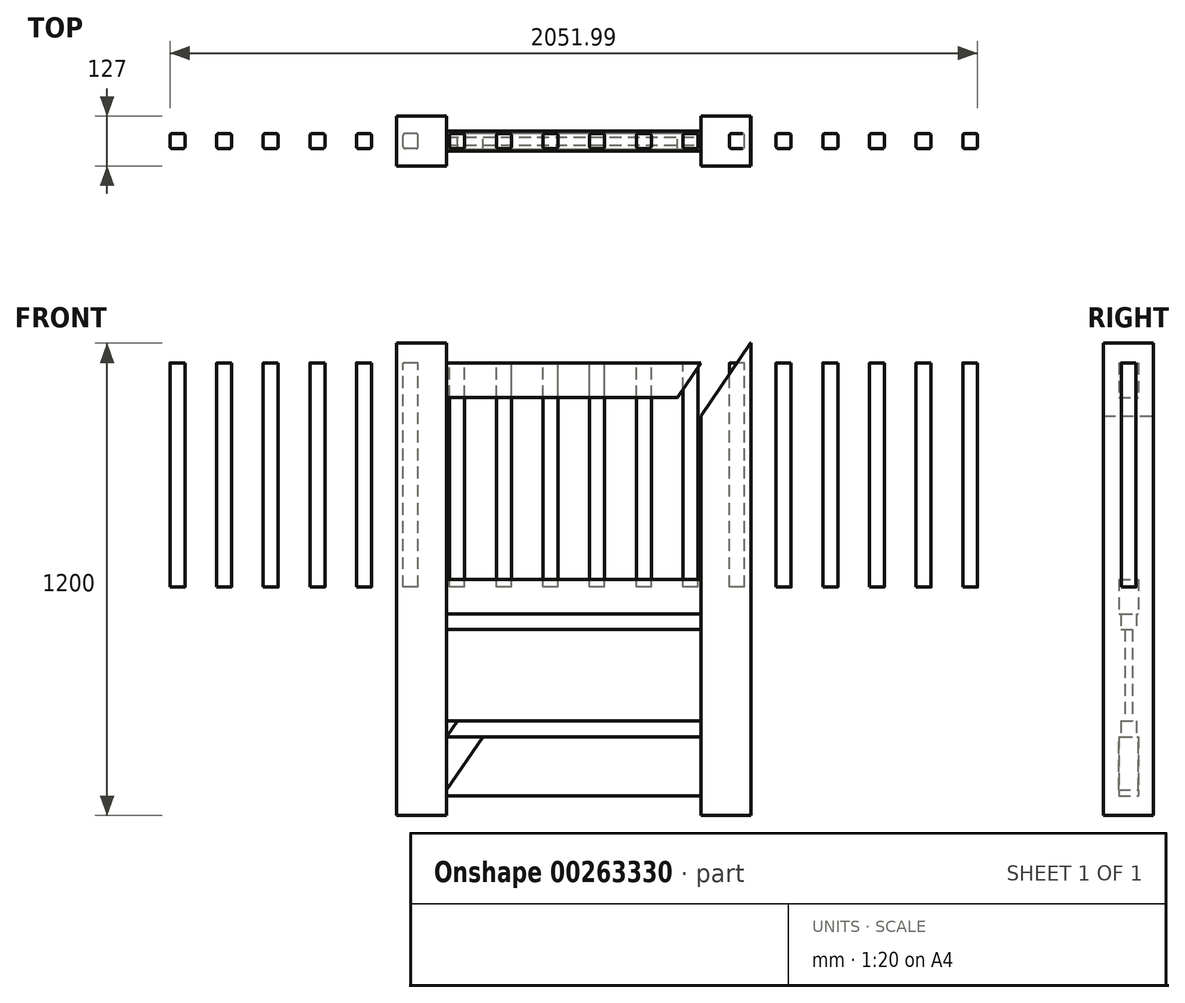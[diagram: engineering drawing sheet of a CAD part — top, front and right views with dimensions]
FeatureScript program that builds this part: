
annotation { "Feature Type Name" : "Feature", "Feature Type Description" : "" }
export const myFeature = defineFeature(function(context is Context, id is Id, definition is map)
    precondition{}
    {
        {
            var Q0;
            Q0=qCreatedBy(makeId("Front.planeOp"),FACE);
            var sketch = newSketch(context, id + "F0", { "sketchPlane" : qUnion([Q0])});
            skLineSegment(sketch, "E0.bottom", {"start": v(450, -600) * mm, "end": v(323, -600) * mm});
            skLineSegment(sketch, "E0.top", {"start": v(450, 600) * mm, "end": v(323, 600) * mm});
            skLineSegment(sketch, "E0.left", {"start": v(450, -600) * mm, "end": v(450, 600) * mm});
            skLineSegment(sketch, "E0.right", {"start": v(-450, -600) * mm, "end": v(-450, 600) * mm});
            skPoint(sketch, "E0.middle", {"position": v(0, 0) * mm});
            skLineSegment(sketch, "E1", {"start": v(-323, 600) * mm, "end": v(-323, -600) * mm});
            skLineSegment(sketch, "E2", {"start": v(323, 600) * mm, "end": v(323, -600) * mm});
            skLineSegment(sketch, "E3", {"start": v(-323, 550) * mm, "end": v(323, 550) * mm});
            skLineSegment(sketch, "E4", {"start": v(-323, 462) * mm, "end": v(323, 462) * mm});
            skLineSegment(sketch, "E5.trimOffspring", {"start": v(-323, 600) * mm, "end": v(-450, 600) * mm});
            skLineSegment(sketch, "E6", {"start": v(-323, 0) * mm, "end": v(323, 0) * mm});
            skLineSegment(sketch, "E7", {"start": v(-323, -88) * mm, "end": v(323, -88) * mm});
            skLineSegment(sketch, "E8", {"start": v(-323, -550) * mm, "end": v(323, -550) * mm});
            skLineSegment(sketch, "E9", {"start": v(-323, -400) * mm, "end": v(323, -400) * mm});
            skLineSegment(sketch, "E10.trimOffspring", {"start": v(-323, -600) * mm, "end": v(-450, -600) * mm});
            skLineSegment(sketch, "E11", {"start": v(-323, -360) * mm, "end": v(323, -360) * mm});
            skLineSegment(sketch, "E12", {"start": v(-323, -128) * mm, "end": v(323, -128) * mm});
            skLineSegment(sketch, "E13", {"start": v(323, 550) * mm, "end": v(-323, -400) * mm});
            skLineSegment(sketch, "E14", {"start": v(-323, -535.16) * mm, "end": v(526.29, 713.8) * mm});
            skSolve(sketch);
        }
        {
            var Q0;
            Q0=makeQuery(id+"F0.imprint","IMPRINT",FACE,{"disambiguationData":[TD([[makeQuery(id+"F0.imprint","IMPRINT",EDGE,{"derivedFrom":sQuery(id+"F0.wireOp",EDGE,"E0.right")}),-1.0]])]});
            var Q1;
            {var subQ8=sQuery(id+"F0.wireOp",EDGE,"E0.bottom");Q1=makeQuery(id+"F0.imprint","IMPRINT",FACE,{"disambiguationData":[TD([[makeQuery(id+"F0.imprint","IMPRINT",EDGE,{"derivedFrom":subQ8}),-1.0]])]});}
            extrude(context, id + "F1", {"entities" : qUnion([Q0, Q1]), "depth" : 63.5 * mm, "hasSecondDirection" : true, "secondDirectionOppositeDirection" : true, "secondDirectionDepth" : 63.5 * mm});
        }
        {
            var Q0;
            {var subQ0=sQuery(id+"F0.wireOp",EDGE,"E8");Q0=makeQuery(id+"F0.imprint","IMPRINT",FACE,{"disambiguationData":[TD([[makeQuery(id+"F0.imprint","IMPRINT",EDGE,{"derivedFrom":subQ0}),1.0]])]});}
            var Q1;
            {var subQ0=sQuery(id+"F0.wireOp",EDGE,"E3");Q1=makeQuery(id+"F0.imprint","IMPRINT",FACE,{"disambiguationData":[TD([[makeQuery(id+"F0.imprint","IMPRINT",EDGE,{"derivedFrom":subQ0}),-1.0]])]});}
            var Q2;
            {var subQ0=sQuery(id+"F0.wireOp",EDGE,"E6");Q2=makeQuery(id+"F0.imprint","IMPRINT",FACE,{"disambiguationData":[TD([[makeQuery(id+"F0.imprint","IMPRINT",EDGE,{"derivedFrom":subQ0}),-1.0]])]});}
            extrude(context, id + "F2", {"entities" : qUnion([Q0, Q1, Q2]), "depth" : 25 * mm, "hasSecondDirection" : true, "secondDirectionOppositeDirection" : true, "secondDirectionDepth" : 25 * mm});
        }
        {
            var Q0;
            {var subQ0=sQuery(id+"F0.wireOp",EDGE,"E7");Q0=makeQuery(id+"F0.imprint","IMPRINT",FACE,{"disambiguationData":[TD([[makeQuery(id+"F0.imprint","IMPRINT",EDGE,{"derivedFrom":subQ0}),-1.0]])]});}
            var Q1;
            {var subQ0=sQuery(id+"F0.wireOp",EDGE,"E9");Q1=makeQuery(id+"F0.imprint","IMPRINT",FACE,{"disambiguationData":[TD([[makeQuery(id+"F0.imprint","IMPRINT",EDGE,{"derivedFrom":subQ0}),1.0]])]});}
            extrude(context, id + "F3", {"entities" : qUnion([Q0, Q1]), "depth" : 20 * mm, "hasSecondDirection" : true, "secondDirectionOppositeDirection" : true, "secondDirectionDepth" : 20 * mm});
        }
        {
            var Q0;
            {var subQ0=sQuery(id+"F0.wireOp",EDGE,"E11");Q0=makeQuery(id+"F0.imprint","IMPRINT",FACE,{"disambiguationData":[TD([[makeQuery(id+"F0.imprint","IMPRINT",EDGE,{"derivedFrom":subQ0}),1.0]])]});}
            extrude(context, id + "F4", {"entities" : qUnion([Q0]), "depth" : 10 * mm, "hasSecondDirection" : true, "secondDirectionOppositeDirection" : true, "secondDirectionDepth" : 10 * mm});
        }
        {
            var Q0;
            Q0=makeQuery(id+"F2.opExtrude","SWEPT_FACE",FACE,{"disambiguationData":[OSD([sQuery(id+"F0.wireOp",EDGE,"E3")])]});
            var sketch = newSketch(context, id + "F5", { "sketchPlane" : qUnion([Q0])});
            skLineSegment(sketch, "E15.bottom", {"start": v(-993.03, -19) * mm, "end": v(-1021.03, -19) * mm});
            skLineSegment(sketch, "E15.top", {"start": v(-993.03, 19) * mm, "end": v(-1021.03, 19) * mm});
            skLineSegment(sketch, "E15.left", {"start": v(-988.03, -14) * mm, "end": v(-988.03, 14) * mm});
            skLineSegment(sketch, "E15.right", {"start": v(-1026.03, -14) * mm, "end": v(-1026.03, 14) * mm});
            skPoint(sketch, "E15.middle", {"position": v(-1007.03, 0) * mm});
            skPoint(sketch, "E16.visualSharp", {"position": v(-1026.03, 19) * mm});
            skArc(sketch, "E16.filletArc", {"start": v(-1021.03, 19) * mm, "mid": v(-1024.57, 17.54) * mm, "end": v(-1026.03, 14) * mm});
            skPoint(sketch, "E17.visualSharp", {"position": v(-1026.03, -19) * mm});
            skArc(sketch, "E17.filletArc", {"start": v(-1026.03, -14) * mm, "mid": v(-1024.57, -17.54) * mm, "end": v(-1021.03, -19) * mm});
            skPoint(sketch, "E18.visualSharp", {"position": v(-988.03, -19) * mm});
            skArc(sketch, "E18.filletArc", {"start": v(-993.03, -19) * mm, "mid": v(-989.5, -17.54) * mm, "end": v(-988.03, -14) * mm});
            skPoint(sketch, "E19.visualSharp", {"position": v(-988.03, 19) * mm});
            skArc(sketch, "E19.filletArc", {"start": v(-988.03, 14) * mm, "mid": v(-989.5, 17.54) * mm, "end": v(-993.03, 19) * mm});
            skLineSegment(sketch, "E20.1.0.0", {"start": v(-874.56, 19) * mm, "end": v(-902.56, 19) * mm});
            skArc(sketch, "E20.1.0.1", {"start": v(-902.56, 19) * mm, "mid": v(-906.1, 17.54) * mm, "end": v(-907.56, 14) * mm});
            skLineSegment(sketch, "E20.1.0.2", {"start": v(-907.56, -14) * mm, "end": v(-907.56, 14) * mm});
            skArc(sketch, "E20.1.0.3", {"start": v(-907.56, -14) * mm, "mid": v(-906.1, -17.54) * mm, "end": v(-902.56, -19) * mm});
            skLineSegment(sketch, "E20.1.0.4", {"start": v(-874.56, -19) * mm, "end": v(-902.56, -19) * mm});
            skArc(sketch, "E20.1.0.5", {"start": v(-874.56, -19) * mm, "mid": v(-871.02, -17.54) * mm, "end": v(-869.56, -14) * mm});
            skLineSegment(sketch, "E20.1.0.6", {"start": v(-869.56, -14) * mm, "end": v(-869.56, 14) * mm});
            skArc(sketch, "E20.1.0.7", {"start": v(-869.56, 14) * mm, "mid": v(-871.02, 17.54) * mm, "end": v(-874.56, 19) * mm});
            skLineSegment(sketch, "E20.2.0.0", {"start": v(-756.1, 19) * mm, "end": v(-784.1, 19) * mm});
            skArc(sketch, "E20.2.0.1", {"start": v(-784.1, 19) * mm, "mid": v(-787.63, 17.54) * mm, "end": v(-789.1, 14) * mm});
            skLineSegment(sketch, "E20.2.0.2", {"start": v(-789.1, -14) * mm, "end": v(-789.1, 14) * mm});
            skArc(sketch, "E20.2.0.3", {"start": v(-789.1, -14) * mm, "mid": v(-787.63, -17.54) * mm, "end": v(-784.1, -19) * mm});
            skLineSegment(sketch, "E20.2.0.4", {"start": v(-756.1, -19) * mm, "end": v(-784.1, -19) * mm});
            skArc(sketch, "E20.2.0.5", {"start": v(-756.1, -19) * mm, "mid": v(-752.55, -17.54) * mm, "end": v(-751.1, -14) * mm});
            skLineSegment(sketch, "E20.2.0.6", {"start": v(-751.1, -14) * mm, "end": v(-751.1, 14) * mm});
            skArc(sketch, "E20.2.0.7", {"start": v(-751.1, 14) * mm, "mid": v(-752.55, 17.54) * mm, "end": v(-756.1, 19) * mm});
            skLineSegment(sketch, "E20.3.0.0", {"start": v(-637.62, 19) * mm, "end": v(-665.62, 19) * mm});
            skArc(sketch, "E20.3.0.1", {"start": v(-665.62, 19) * mm, "mid": v(-669.16, 17.54) * mm, "end": v(-670.62, 14) * mm});
            skLineSegment(sketch, "E20.3.0.2", {"start": v(-670.62, -14) * mm, "end": v(-670.62, 14) * mm});
            skArc(sketch, "E20.3.0.3", {"start": v(-670.62, -14) * mm, "mid": v(-669.16, -17.54) * mm, "end": v(-665.62, -19) * mm});
            skLineSegment(sketch, "E20.3.0.4", {"start": v(-637.62, -19) * mm, "end": v(-665.62, -19) * mm});
            skArc(sketch, "E20.3.0.5", {"start": v(-637.62, -19) * mm, "mid": v(-634.08, -17.54) * mm, "end": v(-632.62, -14) * mm});
            skLineSegment(sketch, "E20.3.0.6", {"start": v(-632.62, -14) * mm, "end": v(-632.62, 14) * mm});
            skArc(sketch, "E20.3.0.7", {"start": v(-632.62, 14) * mm, "mid": v(-634.08, 17.54) * mm, "end": v(-637.62, 19) * mm});
            skLineSegment(sketch, "E20.4.0.0", {"start": v(-519.15, 19) * mm, "end": v(-547.15, 19) * mm});
            skArc(sketch, "E20.4.0.1", {"start": v(-547.15, 19) * mm, "mid": v(-550.69, 17.54) * mm, "end": v(-552.15, 14) * mm});
            skLineSegment(sketch, "E20.4.0.2", {"start": v(-552.15, -14) * mm, "end": v(-552.15, 14) * mm});
            skArc(sketch, "E20.4.0.3", {"start": v(-552.15, -14) * mm, "mid": v(-550.69, -17.54) * mm, "end": v(-547.15, -19) * mm});
            skLineSegment(sketch, "E20.4.0.4", {"start": v(-519.15, -19) * mm, "end": v(-547.15, -19) * mm});
            skArc(sketch, "E20.4.0.5", {"start": v(-519.15, -19) * mm, "mid": v(-515.61, -17.54) * mm, "end": v(-514.15, -14) * mm});
            skLineSegment(sketch, "E20.4.0.6", {"start": v(-514.15, -14) * mm, "end": v(-514.15, 14) * mm});
            skArc(sketch, "E20.4.0.7", {"start": v(-514.15, 14) * mm, "mid": v(-515.61, 17.54) * mm, "end": v(-519.15, 19) * mm});
            skLineSegment(sketch, "E20.5.0.0", {"start": v(-400.68, 19) * mm, "end": v(-428.68, 19) * mm});
            skArc(sketch, "E20.5.0.1", {"start": v(-428.68, 19) * mm, "mid": v(-432.22, 17.54) * mm, "end": v(-433.68, 14) * mm});
            skLineSegment(sketch, "E20.5.0.2", {"start": v(-433.68, -14) * mm, "end": v(-433.68, 14) * mm});
            skArc(sketch, "E20.5.0.3", {"start": v(-433.68, -14) * mm, "mid": v(-432.22, -17.54) * mm, "end": v(-428.68, -19) * mm});
            skLineSegment(sketch, "E20.5.0.4", {"start": v(-400.68, -19) * mm, "end": v(-428.68, -19) * mm});
            skArc(sketch, "E20.5.0.5", {"start": v(-400.68, -19) * mm, "mid": v(-397.14, -17.54) * mm, "end": v(-395.68, -14) * mm});
            skLineSegment(sketch, "E20.5.0.6", {"start": v(-395.68, -14) * mm, "end": v(-395.68, 14) * mm});
            skArc(sketch, "E20.5.0.7", {"start": v(-395.68, 14) * mm, "mid": v(-397.14, 17.54) * mm, "end": v(-400.68, 19) * mm});
            skLineSegment(sketch, "E20.6.0.0", {"start": v(-282.21, 19) * mm, "end": v(-310.21, 19) * mm});
            skArc(sketch, "E20.6.0.1", {"start": v(-310.21, 19) * mm, "mid": v(-313.75, 17.54) * mm, "end": v(-315.21, 14) * mm});
            skLineSegment(sketch, "E20.6.0.2", {"start": v(-315.21, -14) * mm, "end": v(-315.21, 14) * mm});
            skArc(sketch, "E20.6.0.3", {"start": v(-315.21, -14) * mm, "mid": v(-313.75, -17.54) * mm, "end": v(-310.21, -19) * mm});
            skLineSegment(sketch, "E20.6.0.4", {"start": v(-282.21, -19) * mm, "end": v(-310.21, -19) * mm});
            skArc(sketch, "E20.6.0.5", {"start": v(-282.21, -19) * mm, "mid": v(-278.67, -17.54) * mm, "end": v(-277.21, -14) * mm});
            skLineSegment(sketch, "E20.6.0.6", {"start": v(-277.21, -14) * mm, "end": v(-277.21, 14) * mm});
            skArc(sketch, "E20.6.0.7", {"start": v(-277.21, 14) * mm, "mid": v(-278.67, 17.54) * mm, "end": v(-282.21, 19) * mm});
            skLineSegment(sketch, "E20.7.0.0", {"start": v(-163.74, 19) * mm, "end": v(-191.74, 19) * mm});
            skArc(sketch, "E20.7.0.1", {"start": v(-191.74, 19) * mm, "mid": v(-195.28, 17.54) * mm, "end": v(-196.74, 14) * mm});
            skLineSegment(sketch, "E20.7.0.2", {"start": v(-196.74, -14) * mm, "end": v(-196.74, 14) * mm});
            skArc(sketch, "E20.7.0.3", {"start": v(-196.74, -14) * mm, "mid": v(-195.28, -17.54) * mm, "end": v(-191.74, -19) * mm});
            skLineSegment(sketch, "E20.7.0.4", {"start": v(-163.74, -19) * mm, "end": v(-191.74, -19) * mm});
            skArc(sketch, "E20.7.0.5", {"start": v(-163.74, -19) * mm, "mid": v(-160.2, -17.54) * mm, "end": v(-158.74, -14) * mm});
            skLineSegment(sketch, "E20.7.0.6", {"start": v(-158.74, -14) * mm, "end": v(-158.74, 14) * mm});
            skArc(sketch, "E20.7.0.7", {"start": v(-158.74, 14) * mm, "mid": v(-160.2, 17.54) * mm, "end": v(-163.74, 19) * mm});
            skLineSegment(sketch, "E20.8.0.0", {"start": v(-45.27, 19) * mm, "end": v(-73.27, 19) * mm});
            skArc(sketch, "E20.8.0.1", {"start": v(-73.27, 19) * mm, "mid": v(-76.8, 17.54) * mm, "end": v(-78.27, 14) * mm});
            skLineSegment(sketch, "E20.8.0.2", {"start": v(-78.27, -14) * mm, "end": v(-78.27, 14) * mm});
            skArc(sketch, "E20.8.0.3", {"start": v(-78.27, -14) * mm, "mid": v(-76.8, -17.54) * mm, "end": v(-73.27, -19) * mm});
            skLineSegment(sketch, "E20.8.0.4", {"start": v(-45.27, -19) * mm, "end": v(-73.27, -19) * mm});
            skArc(sketch, "E20.8.0.5", {"start": v(-45.27, -19) * mm, "mid": v(-41.73, -17.54) * mm, "end": v(-40.27, -14) * mm});
            skLineSegment(sketch, "E20.8.0.6", {"start": v(-40.27, -14) * mm, "end": v(-40.27, 14) * mm});
            skArc(sketch, "E20.8.0.7", {"start": v(-40.27, 14) * mm, "mid": v(-41.73, 17.54) * mm, "end": v(-45.27, 19) * mm});
            skLineSegment(sketch, "E20.9.0.0", {"start": v(73.2, 19) * mm, "end": v(45.2, 19) * mm});
            skArc(sketch, "E20.9.0.1", {"start": v(45.2, 19) * mm, "mid": v(41.66, 17.54) * mm, "end": v(40.2, 14) * mm});
            skLineSegment(sketch, "E20.9.0.2", {"start": v(40.2, -14) * mm, "end": v(40.2, 14) * mm});
            skArc(sketch, "E20.9.0.3", {"start": v(40.2, -14) * mm, "mid": v(41.66, -17.54) * mm, "end": v(45.2, -19) * mm});
            skLineSegment(sketch, "E20.9.0.4", {"start": v(73.2, -19) * mm, "end": v(45.2, -19) * mm});
            skArc(sketch, "E20.9.0.5", {"start": v(73.2, -19) * mm, "mid": v(76.74, -17.54) * mm, "end": v(78.2, -14) * mm});
            skLineSegment(sketch, "E20.9.0.6", {"start": v(78.2, -14) * mm, "end": v(78.2, 14) * mm});
            skArc(sketch, "E20.9.0.7", {"start": v(78.2, 14) * mm, "mid": v(76.74, 17.54) * mm, "end": v(73.2, 19) * mm});
            skLineSegment(sketch, "E20.10.0.0", {"start": v(191.67, 19) * mm, "end": v(163.67, 19) * mm});
            skArc(sketch, "E20.10.0.1", {"start": v(163.67, 19) * mm, "mid": v(160.13, 17.54) * mm, "end": v(158.67, 14) * mm});
            skLineSegment(sketch, "E20.10.0.2", {"start": v(158.67, -14) * mm, "end": v(158.67, 14) * mm});
            skArc(sketch, "E20.10.0.3", {"start": v(158.67, -14) * mm, "mid": v(160.13, -17.54) * mm, "end": v(163.67, -19) * mm});
            skLineSegment(sketch, "E20.10.0.4", {"start": v(191.67, -19) * mm, "end": v(163.67, -19) * mm});
            skArc(sketch, "E20.10.0.5", {"start": v(191.67, -19) * mm, "mid": v(195.2, -17.54) * mm, "end": v(196.67, -14) * mm});
            skLineSegment(sketch, "E20.10.0.6", {"start": v(196.67, -14) * mm, "end": v(196.67, 14) * mm});
            skArc(sketch, "E20.10.0.7", {"start": v(196.67, 14) * mm, "mid": v(195.2, 17.54) * mm, "end": v(191.67, 19) * mm});
            skLineSegment(sketch, "E20.11.0.0", {"start": v(310.14, 19) * mm, "end": v(282.14, 19) * mm});
            skArc(sketch, "E20.11.0.1", {"start": v(282.14, 19) * mm, "mid": v(278.6, 17.54) * mm, "end": v(277.14, 14) * mm});
            skLineSegment(sketch, "E20.11.0.2", {"start": v(277.14, -14) * mm, "end": v(277.14, 14) * mm});
            skArc(sketch, "E20.11.0.3", {"start": v(277.14, -14) * mm, "mid": v(278.6, -17.54) * mm, "end": v(282.14, -19) * mm});
            skLineSegment(sketch, "E20.11.0.4", {"start": v(310.14, -19) * mm, "end": v(282.14, -19) * mm});
            skArc(sketch, "E20.11.0.5", {"start": v(310.14, -19) * mm, "mid": v(313.68, -17.54) * mm, "end": v(315.14, -14) * mm});
            skLineSegment(sketch, "E20.11.0.6", {"start": v(315.14, -14) * mm, "end": v(315.14, 14) * mm});
            skArc(sketch, "E20.11.0.7", {"start": v(315.14, 14) * mm, "mid": v(313.68, 17.54) * mm, "end": v(310.14, 19) * mm});
            skLineSegment(sketch, "E20.12.0.0", {"start": v(428.6, 19) * mm, "end": v(400.6, 19) * mm});
            skArc(sketch, "E20.12.0.1", {"start": v(400.6, 19) * mm, "mid": v(397.07, 17.54) * mm, "end": v(395.6, 14) * mm});
            skLineSegment(sketch, "E20.12.0.2", {"start": v(395.6, -14) * mm, "end": v(395.6, 14) * mm});
            skArc(sketch, "E20.12.0.3", {"start": v(395.6, -14) * mm, "mid": v(397.07, -17.54) * mm, "end": v(400.6, -19) * mm});
            skLineSegment(sketch, "E20.12.0.4", {"start": v(428.6, -19) * mm, "end": v(400.6, -19) * mm});
            skArc(sketch, "E20.12.0.5", {"start": v(428.6, -19) * mm, "mid": v(432.15, -17.54) * mm, "end": v(433.6, -14) * mm});
            skLineSegment(sketch, "E20.12.0.6", {"start": v(433.6, -14) * mm, "end": v(433.6, 14) * mm});
            skArc(sketch, "E20.12.0.7", {"start": v(433.6, 14) * mm, "mid": v(432.15, 17.54) * mm, "end": v(428.6, 19) * mm});
            skLineSegment(sketch, "E20.13.0.0", {"start": v(547.08, 19) * mm, "end": v(519.08, 19) * mm});
            skArc(sketch, "E20.13.0.1", {"start": v(519.08, 19) * mm, "mid": v(515.54, 17.54) * mm, "end": v(514.08, 14) * mm});
            skLineSegment(sketch, "E20.13.0.2", {"start": v(514.08, -14) * mm, "end": v(514.08, 14) * mm});
            skArc(sketch, "E20.13.0.3", {"start": v(514.08, -14) * mm, "mid": v(515.54, -17.54) * mm, "end": v(519.08, -19) * mm});
            skLineSegment(sketch, "E20.13.0.4", {"start": v(547.08, -19) * mm, "end": v(519.08, -19) * mm});
            skArc(sketch, "E20.13.0.5", {"start": v(547.08, -19) * mm, "mid": v(550.62, -17.54) * mm, "end": v(552.08, -14) * mm});
            skLineSegment(sketch, "E20.13.0.6", {"start": v(552.08, -14) * mm, "end": v(552.08, 14) * mm});
            skArc(sketch, "E20.13.0.7", {"start": v(552.08, 14) * mm, "mid": v(550.62, 17.54) * mm, "end": v(547.08, 19) * mm});
            skLineSegment(sketch, "E20.14.0.0", {"start": v(665.55, 19) * mm, "end": v(637.55, 19) * mm});
            skArc(sketch, "E20.14.0.1", {"start": v(637.55, 19) * mm, "mid": v(634.01, 17.54) * mm, "end": v(632.55, 14) * mm});
            skLineSegment(sketch, "E20.14.0.2", {"start": v(632.55, -14) * mm, "end": v(632.55, 14) * mm});
            skArc(sketch, "E20.14.0.3", {"start": v(632.55, -14) * mm, "mid": v(634.01, -17.54) * mm, "end": v(637.55, -19) * mm});
            skLineSegment(sketch, "E20.14.0.4", {"start": v(665.55, -19) * mm, "end": v(637.55, -19) * mm});
            skArc(sketch, "E20.14.0.5", {"start": v(665.55, -19) * mm, "mid": v(669.09, -17.54) * mm, "end": v(670.55, -14) * mm});
            skLineSegment(sketch, "E20.14.0.6", {"start": v(670.55, -14) * mm, "end": v(670.55, 14) * mm});
            skArc(sketch, "E20.14.0.7", {"start": v(670.55, 14) * mm, "mid": v(669.09, 17.54) * mm, "end": v(665.55, 19) * mm});
            skLineSegment(sketch, "E20.15.0.0", {"start": v(784.02, 19) * mm, "end": v(756.02, 19) * mm});
            skArc(sketch, "E20.15.0.1", {"start": v(756.02, 19) * mm, "mid": v(752.48, 17.54) * mm, "end": v(751.02, 14) * mm});
            skLineSegment(sketch, "E20.15.0.2", {"start": v(751.02, -14) * mm, "end": v(751.02, 14) * mm});
            skArc(sketch, "E20.15.0.3", {"start": v(751.02, -14) * mm, "mid": v(752.48, -17.54) * mm, "end": v(756.02, -19) * mm});
            skLineSegment(sketch, "E20.15.0.4", {"start": v(784.02, -19) * mm, "end": v(756.02, -19) * mm});
            skArc(sketch, "E20.15.0.5", {"start": v(784.02, -19) * mm, "mid": v(787.56, -17.54) * mm, "end": v(789.02, -14) * mm});
            skLineSegment(sketch, "E20.15.0.6", {"start": v(789.02, -14) * mm, "end": v(789.02, 14) * mm});
            skArc(sketch, "E20.15.0.7", {"start": v(789.02, 14) * mm, "mid": v(787.56, 17.54) * mm, "end": v(784.02, 19) * mm});
            skLineSegment(sketch, "E20.16.0.0", {"start": v(902.49, 19) * mm, "end": v(874.49, 19) * mm});
            skArc(sketch, "E20.16.0.1", {"start": v(874.49, 19) * mm, "mid": v(870.95, 17.54) * mm, "end": v(869.49, 14) * mm});
            skLineSegment(sketch, "E20.16.0.2", {"start": v(869.49, -14) * mm, "end": v(869.49, 14) * mm});
            skArc(sketch, "E20.16.0.3", {"start": v(869.49, -14) * mm, "mid": v(870.95, -17.54) * mm, "end": v(874.49, -19) * mm});
            skLineSegment(sketch, "E20.16.0.4", {"start": v(902.49, -19) * mm, "end": v(874.49, -19) * mm});
            skArc(sketch, "E20.16.0.5", {"start": v(902.49, -19) * mm, "mid": v(906.03, -17.54) * mm, "end": v(907.49, -14) * mm});
            skLineSegment(sketch, "E20.16.0.6", {"start": v(907.49, -14) * mm, "end": v(907.49, 14) * mm});
            skArc(sketch, "E20.16.0.7", {"start": v(907.49, 14) * mm, "mid": v(906.03, 17.54) * mm, "end": v(902.49, 19) * mm});
            skLineSegment(sketch, "E20.17.0.0", {"start": v(1020.96, 19) * mm, "end": v(992.96, 19) * mm});
            skArc(sketch, "E20.17.0.1", {"start": v(992.96, 19) * mm, "mid": v(989.42, 17.54) * mm, "end": v(987.96, 14) * mm});
            skLineSegment(sketch, "E20.17.0.2", {"start": v(987.96, -14) * mm, "end": v(987.96, 14) * mm});
            skArc(sketch, "E20.17.0.3", {"start": v(987.96, -14) * mm, "mid": v(989.42, -17.54) * mm, "end": v(992.96, -19) * mm});
            skLineSegment(sketch, "E20.17.0.4", {"start": v(1020.96, -19) * mm, "end": v(992.96, -19) * mm});
            skArc(sketch, "E20.17.0.5", {"start": v(1020.96, -19) * mm, "mid": v(1024.5, -17.54) * mm, "end": v(1025.96, -14) * mm});
            skLineSegment(sketch, "E20.17.0.6", {"start": v(1025.96, -14) * mm, "end": v(1025.96, 14) * mm});
            skArc(sketch, "E20.17.0.7", {"start": v(1025.96, 14) * mm, "mid": v(1024.5, 17.54) * mm, "end": v(1020.96, 19) * mm});
            skLineSegment(sketch, "E20.direction1", {"start": v(-1021.03, 19) * mm, "end": v(-902.56, 19) * mm, "construction": true});
            skSolve(sketch);
        }
        {
            var Q0;
            Q0=makeQuery(id+"F5.imprint","IMPRINT",FACE,{"disambiguationData":[TD([[makeQuery(id+"F5.imprint","IMPRINT",EDGE,{"derivedFrom":sQuery(id+"F5.wireOp",EDGE,"E15.bottom")}),-1.0]])]});
            var Q1;
            Q1=makeQuery(id+"F5.imprint","IMPRINT",FACE,{"disambiguationData":[TD([[makeQuery(id+"F5.imprint","IMPRINT",EDGE,{"derivedFrom":sQuery(id+"F5.wireOp",EDGE,"E20.1.0.0")}),1.0]])]});
            var Q2;
            Q2=makeQuery(id+"F5.imprint","IMPRINT",FACE,{"disambiguationData":[TD([[makeQuery(id+"F5.imprint","IMPRINT",EDGE,{"derivedFrom":sQuery(id+"F5.wireOp",EDGE,"E20.2.0.0")}),1.0]])]});
            var Q3;
            Q3=makeQuery(id+"F5.imprint","IMPRINT",FACE,{"disambiguationData":[TD([[makeQuery(id+"F5.imprint","IMPRINT",EDGE,{"derivedFrom":sQuery(id+"F5.wireOp",EDGE,"E20.3.0.0")}),1.0]])]});
            var Q4;
            Q4=makeQuery(id+"F5.imprint","IMPRINT",FACE,{"disambiguationData":[TD([[makeQuery(id+"F5.imprint","IMPRINT",EDGE,{"derivedFrom":sQuery(id+"F5.wireOp",EDGE,"E20.4.0.0")}),1.0]])]});
            var Q5;
            Q5=makeQuery(id+"F5.imprint","IMPRINT",FACE,{"disambiguationData":[TD([[makeQuery(id+"F5.imprint","IMPRINT",EDGE,{"derivedFrom":sQuery(id+"F5.wireOp",EDGE,"E20.5.0.0")}),1.0]])]});
            var Q6;
            Q6=makeQuery(id+"F5.imprint","IMPRINT",FACE,{"disambiguationData":[TD([[makeQuery(id+"F5.imprint","IMPRINT",EDGE,{"derivedFrom":sQuery(id+"F5.wireOp",EDGE,"E20.6.0.0")}),1.0]])]});
            var Q7;
            Q7=makeQuery(id+"F5.imprint","IMPRINT",FACE,{"disambiguationData":[TD([[makeQuery(id+"F5.imprint","IMPRINT",EDGE,{"derivedFrom":sQuery(id+"F5.wireOp",EDGE,"E20.7.0.0")}),1.0]])]});
            var Q8;
            Q8=makeQuery(id+"F5.imprint","IMPRINT",FACE,{"disambiguationData":[TD([[makeQuery(id+"F5.imprint","IMPRINT",EDGE,{"derivedFrom":sQuery(id+"F5.wireOp",EDGE,"E20.8.0.0")}),1.0]])]});
            var Q9;
            Q9=makeQuery(id+"F5.imprint","IMPRINT",FACE,{"disambiguationData":[TD([[makeQuery(id+"F5.imprint","IMPRINT",EDGE,{"derivedFrom":sQuery(id+"F5.wireOp",EDGE,"E20.9.0.0")}),1.0]])]});
            var Q10;
            Q10=makeQuery(id+"F5.imprint","IMPRINT",FACE,{"disambiguationData":[TD([[makeQuery(id+"F5.imprint","IMPRINT",EDGE,{"derivedFrom":sQuery(id+"F5.wireOp",EDGE,"E20.10.0.0")}),1.0]])]});
            var Q11;
            Q11=makeQuery(id+"F5.imprint","IMPRINT",FACE,{"disambiguationData":[TD([[makeQuery(id+"F5.imprint","IMPRINT",EDGE,{"derivedFrom":sQuery(id+"F5.wireOp",EDGE,"E20.11.0.0")}),1.0]])]});
            var Q12;
            Q12=makeQuery(id+"F5.imprint","IMPRINT",FACE,{"disambiguationData":[TD([[makeQuery(id+"F5.imprint","IMPRINT",EDGE,{"derivedFrom":sQuery(id+"F5.wireOp",EDGE,"E20.12.0.0")}),1.0]])]});
            var Q13;
            Q13=makeQuery(id+"F5.imprint","IMPRINT",FACE,{"disambiguationData":[TD([[makeQuery(id+"F5.imprint","IMPRINT",EDGE,{"derivedFrom":sQuery(id+"F5.wireOp",EDGE,"E20.13.0.0")}),1.0]])]});
            var Q14;
            Q14=makeQuery(id+"F5.imprint","IMPRINT",FACE,{"disambiguationData":[TD([[makeQuery(id+"F5.imprint","IMPRINT",EDGE,{"derivedFrom":sQuery(id+"F5.wireOp",EDGE,"E20.14.0.0")}),1.0]])]});
            var Q15;
            Q15=makeQuery(id+"F5.imprint","IMPRINT",FACE,{"disambiguationData":[TD([[makeQuery(id+"F5.imprint","IMPRINT",EDGE,{"derivedFrom":sQuery(id+"F5.wireOp",EDGE,"E20.15.0.0")}),1.0]])]});
            var Q16;
            Q16=makeQuery(id+"F5.imprint","IMPRINT",FACE,{"disambiguationData":[TD([[makeQuery(id+"F5.imprint","IMPRINT",EDGE,{"derivedFrom":sQuery(id+"F5.wireOp",EDGE,"E20.16.0.0")}),1.0]])]});
            var Q17;
            Q17=makeQuery(id+"F5.imprint","IMPRINT",FACE,{"disambiguationData":[TD([[makeQuery(id+"F5.imprint","IMPRINT",EDGE,{"derivedFrom":sQuery(id+"F5.wireOp",EDGE,"E20.17.0.0")}),1.0]])]});
            extrude(context, id + "F6", {"entities" : qUnion([Q0, Q1, Q2, Q3, Q4, Q5, Q6, Q7, Q8, Q9, Q10, Q11, Q12, Q13, Q14, Q15, Q16, Q17]), "oppositeDirection" : true, "depth" : 570 * mm});
        }
    });
